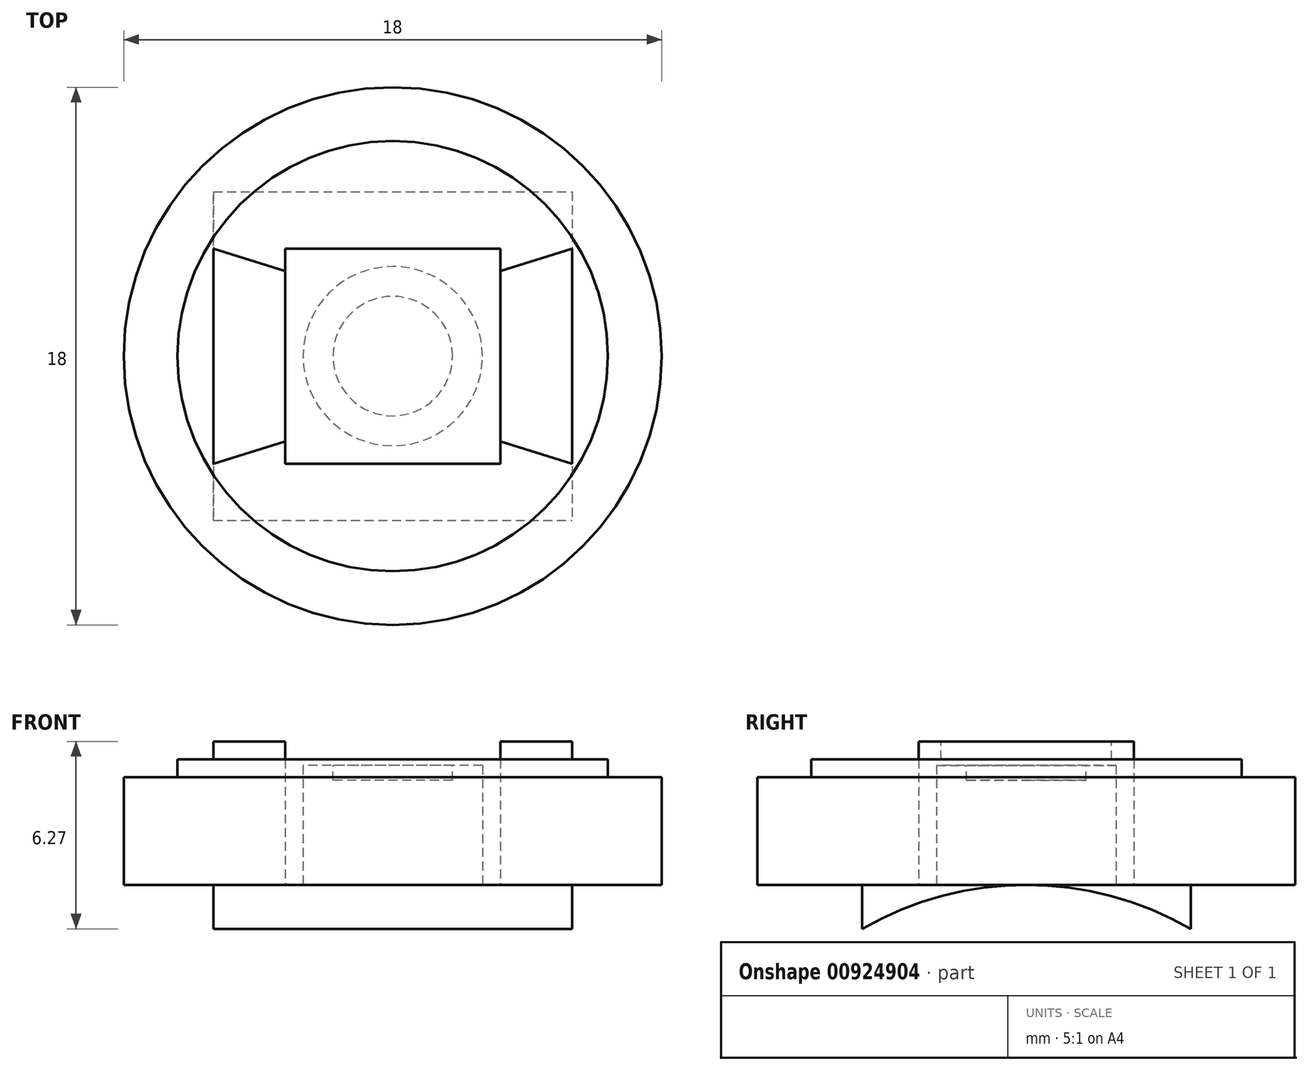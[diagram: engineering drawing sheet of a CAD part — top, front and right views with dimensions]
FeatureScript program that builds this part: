
annotation { "Feature Type Name" : "Feature", "Feature Type Description" : "" }
export const myFeature = defineFeature(function(context is Context, id is Id, definition is map)
    precondition{}
    {
        {
            var Q0;
            Q0=qCreatedBy(makeId("Top.planeOp"),FACE);
            var sketch = newSketch(context, id + "F0", { "sketchPlane" : qUnion([Q0])});
            skCircle(sketch, "E0", {"center": v(0, 0) * mm, "radius": 7.5 * mm});
            skCircle(sketch, "E1", {"center": v(0, 0) * mm, "radius": 6 * mm});
            skCircle(sketch, "E2", {"center": v(0, 0) * mm, "radius": 3 * mm});
            skLineSegment(sketch, "E3", {"start": v(0, 7.5) * mm, "end": v(0, 0) * mm});
            skLineSegment(sketch, "E4", {"start": v(0, 0) * mm, "end": v(0, -7.5) * mm});
            skLineSegment(sketch, "E5", {"start": v(0, 0) * mm, "end": v(7.5, 0) * mm});
            skLineSegment(sketch, "E6", {"start": v(0, 0) * mm, "end": v(-7.5, 0) * mm});
            skLineSegment(sketch, "E7.bottom", {"start": v(3, 3) * mm, "end": v(-3, 3) * mm});
            skLineSegment(sketch, "E7.top", {"start": v(3, -3) * mm, "end": v(-3, -3) * mm});
            skLineSegment(sketch, "E7.left", {"start": v(3, 3) * mm, "end": v(3, -3) * mm});
            skLineSegment(sketch, "E7.right", {"start": v(-3, 3) * mm, "end": v(-3, -3) * mm});
            skLineSegment(sketch, "E8.bottom", {"start": v(-3, 3) * mm, "end": v(3, 3) * mm});
            skLineSegment(sketch, "E8.top", {"start": v(-3, 5) * mm, "end": v(3, 5) * mm});
            skLineSegment(sketch, "E8.left", {"start": v(-3, 3) * mm, "end": v(-3, 5) * mm});
            skLineSegment(sketch, "E8.right", {"start": v(3, 3) * mm, "end": v(3, 5) * mm});
            skLineSegment(sketch, "E9.bottom", {"start": v(-3, -3) * mm, "end": v(3, -3) * mm});
            skLineSegment(sketch, "E9.top", {"start": v(-3, -5) * mm, "end": v(3, -5) * mm});
            skLineSegment(sketch, "E9.left", {"start": v(-3, -3) * mm, "end": v(-3, -5) * mm});
            skLineSegment(sketch, "E9.right", {"start": v(3, -3) * mm, "end": v(3, -5) * mm});
            skSolve(sketch);
        }
        {
            var Q0;
            {var subQ0=sQuery(id+"F0.wireOp",EDGE,"E4");var subQ1=sQuery(id+"F0.wireOp",EDGE,"E0");var subQ2=makeQuery(id+"F0.imprint","INTERSECT",VERTEX,{"derivedFrom":[subQ1,subQ0]});Q0=makeQuery(id+"F0.imprint","IMPRINT",FACE,{"disambiguationData":[TD([[makeQuery(id+"F0.imprint","IMPRINT",EDGE,{"disambiguationData":[TD([[subQ2,-1.0]])],"derivedFrom":subQ1}),1.0]])]});}
            var Q1;
            {var subQ0=sQuery(id+"F0.wireOp",EDGE,"E4");var subQ1=sQuery(id+"F0.wireOp",EDGE,"E0");var subQ2=makeQuery(id+"F0.imprint","INTERSECT",VERTEX,{"derivedFrom":[subQ1,subQ0]});Q1=makeQuery(id+"F0.imprint","IMPRINT",FACE,{"disambiguationData":[TD([[makeQuery(id+"F0.imprint","IMPRINT",EDGE,{"disambiguationData":[TD([[subQ2,1.0]])],"derivedFrom":subQ1}),1.0]])]});}
            var Q2;
            {var subQ0=sQuery(id+"F0.wireOp",EDGE,"E3");var subQ1=sQuery(id+"F0.wireOp",EDGE,"E0");var subQ2=makeQuery(id+"F0.imprint","INTERSECT",VERTEX,{"derivedFrom":[subQ1,subQ0]});Q2=makeQuery(id+"F0.imprint","IMPRINT",FACE,{"disambiguationData":[TD([[makeQuery(id+"F0.imprint","IMPRINT",EDGE,{"disambiguationData":[TD([[subQ2,-1.0]])],"derivedFrom":subQ1}),1.0]])]});}
            var Q3;
            {var subQ0=sQuery(id+"F0.wireOp",EDGE,"E3");var subQ1=sQuery(id+"F0.wireOp",EDGE,"E0");var subQ2=makeQuery(id+"F0.imprint","INTERSECT",VERTEX,{"derivedFrom":[subQ1,subQ0]});Q3=makeQuery(id+"F0.imprint","IMPRINT",FACE,{"disambiguationData":[TD([[makeQuery(id+"F0.imprint","IMPRINT",EDGE,{"disambiguationData":[TD([[subQ2,1.0]])],"derivedFrom":subQ1}),1.0]])]});}
            extrude(context, id + "F1", {"entities" : qUnion([Q0, Q1, Q2, Q3]), "depth" : 3 * mm, "offsetDistance" : 25 * mm});
        }
        {
            var Q0;
            {var subQ9=sQuery(id+"F0.wireOp",EDGE,"E9.right");Q0=makeQuery(id+"F0.imprint","IMPRINT",FACE,{"disambiguationData":[TD([[makeQuery(id+"F0.imprint","IMPRINT",EDGE,{"derivedFrom":subQ9}),1.0]])]});}
            var Q1;
            {var subQ0=sQuery(id+"F0.wireOp",EDGE,"E8.right");Q1=makeQuery(id+"F0.imprint","IMPRINT",FACE,{"disambiguationData":[TD([[makeQuery(id+"F0.imprint","IMPRINT",EDGE,{"derivedFrom":subQ0}),-1.0]])]});}
            var Q2;
            {var subQ9=sQuery(id+"F0.wireOp",EDGE,"E8.left");Q2=makeQuery(id+"F0.imprint","IMPRINT",FACE,{"disambiguationData":[TD([[makeQuery(id+"F0.imprint","IMPRINT",EDGE,{"derivedFrom":subQ9}),1.0]])]});}
            var Q3;
            {var subQ0=sQuery(id+"F0.wireOp",EDGE,"E9.left");Q3=makeQuery(id+"F0.imprint","IMPRINT",FACE,{"disambiguationData":[TD([[makeQuery(id+"F0.imprint","IMPRINT",EDGE,{"derivedFrom":subQ0}),-1.0]])]});}
            extrude(context, id + "F2", {"entities" : qUnion([Q0, Q1, Q2, Q3]), "operationType" : NewBodyOperationType.ADD, "depth" : 3.5 * mm, "offsetDistance" : 25 * mm});
        }
        {
            var Q0;
            {var subQ0=sQuery(id+"F0.wireOp",EDGE,"E5");var subQ1=sQuery(id+"F0.wireOp",EDGE,"E2");var subQ2=makeQuery(id+"F0.imprint","INTERSECT",VERTEX,{"derivedFrom":[subQ1,subQ0,sQuery(id+"F0.wireOp",EDGE,"E7.left")]});Q0=makeQuery(id+"F0.imprint","IMPRINT",FACE,{"disambiguationData":[TD([[makeQuery(id+"F0.imprint","IMPRINT",EDGE,{"disambiguationData":[TD([[subQ2,1.0]])],"derivedFrom":subQ1}),1.0]])]});}
            var Q1;
            {var subQ5=sQuery(id+"F0.wireOp",EDGE,"E9.right");Q1=makeQuery(id+"F0.imprint","IMPRINT",FACE,{"disambiguationData":[TD([[makeQuery(id+"F0.imprint","IMPRINT",EDGE,{"derivedFrom":subQ5}),-1.0]])]});}
            var Q2;
            {var subQ5=sQuery(id+"F0.wireOp",EDGE,"E9.left");Q2=makeQuery(id+"F0.imprint","IMPRINT",FACE,{"disambiguationData":[TD([[makeQuery(id+"F0.imprint","IMPRINT",EDGE,{"derivedFrom":subQ5}),1.0]])]});}
            var Q3;
            {var subQ0=sQuery(id+"F0.wireOp",EDGE,"E6");var subQ1=sQuery(id+"F0.wireOp",EDGE,"E2");var subQ2=makeQuery(id+"F0.imprint","INTERSECT",VERTEX,{"derivedFrom":[subQ1,subQ0,sQuery(id+"F0.wireOp",EDGE,"E7.right")]});Q3=makeQuery(id+"F0.imprint","IMPRINT",FACE,{"disambiguationData":[TD([[makeQuery(id+"F0.imprint","IMPRINT",EDGE,{"disambiguationData":[TD([[subQ2,-1.0]])],"derivedFrom":subQ1}),1.0]])]});}
            var Q4;
            {var subQ0=sQuery(id+"F0.wireOp",EDGE,"E3");var subQ1=sQuery(id+"F0.wireOp",EDGE,"E2");var subQ2=makeQuery(id+"F0.imprint","INTERSECT",VERTEX,{"derivedFrom":[subQ1,subQ0,sQuery(id+"F0.wireOp",EDGE,"E8.bottom")]});Q4=makeQuery(id+"F0.imprint","IMPRINT",FACE,{"disambiguationData":[TD([[makeQuery(id+"F0.imprint","IMPRINT",EDGE,{"disambiguationData":[TD([[subQ2,-1.0]])],"derivedFrom":subQ1}),1.0]])]});}
            var Q5;
            {var subQ5=sQuery(id+"F0.wireOp",EDGE,"E8.right");Q5=makeQuery(id+"F0.imprint","IMPRINT",FACE,{"disambiguationData":[TD([[makeQuery(id+"F0.imprint","IMPRINT",EDGE,{"derivedFrom":subQ5}),1.0]])]});}
            var Q6;
            {var subQ5=sQuery(id+"F0.wireOp",EDGE,"E8.left");Q6=makeQuery(id+"F0.imprint","IMPRINT",FACE,{"disambiguationData":[TD([[makeQuery(id+"F0.imprint","IMPRINT",EDGE,{"derivedFrom":subQ5}),-1.0]])]});}
            var Q7;
            {var subQ0=sQuery(id+"F0.wireOp",EDGE,"E3");var subQ1=sQuery(id+"F0.wireOp",EDGE,"E2");var subQ2=makeQuery(id+"F0.imprint","INTERSECT",VERTEX,{"derivedFrom":[subQ1,subQ0,sQuery(id+"F0.wireOp",EDGE,"E8.bottom")]});Q7=makeQuery(id+"F0.imprint","IMPRINT",FACE,{"disambiguationData":[TD([[makeQuery(id+"F0.imprint","IMPRINT",EDGE,{"disambiguationData":[TD([[subQ2,1.0]])],"derivedFrom":subQ1}),1.0]])]});}
            extrude(context, id + "F3", {"entities" : qUnion([Q0, Q1, Q2, Q3, Q4, Q5, Q6, Q7]), "operationType" : NewBodyOperationType.ADD, "depth" : 4 * mm, "offsetDistance" : 25 * mm});
        }
        {
            var Q0;
            Q0=makeQuery(id+"F2.opExtrude","CAP_FACE",FACE,{"disambiguationData":[OSD([sQuery(id+"F0.wireOp",EDGE,"E1"),sQuery(id+"F0.wireOp",EDGE,"E7.left"),sQuery(id+"F0.wireOp",EDGE,"E7.right"),sQuery(id+"F0.wireOp",EDGE,"E8.top"),sQuery(id+"F0.wireOp",EDGE,"E8.left"),sQuery(id+"F0.wireOp",EDGE,"E8.right"),sQuery(id+"F0.wireOp",EDGE,"E9.top"),sQuery(id+"F0.wireOp",EDGE,"E9.left"),sQuery(id+"F0.wireOp",EDGE,"E9.right")])],"isStart":false});
            var sketch = newSketch(context, id + "F4", { "sketchPlane" : qUnion([Q0])});
            skLineSegment(sketch, "E10.bottom", {"start": v(3, -3) * mm, "end": v(-3, -3) * mm});
            skLineSegment(sketch, "E10.top", {"start": v(3, 3) * mm, "end": v(-3, 3) * mm});
            skLineSegment(sketch, "E10.left", {"start": v(3, -3) * mm, "end": v(3, 3) * mm});
            skLineSegment(sketch, "E10.right", {"start": v(-3, -3) * mm, "end": v(-3, 3) * mm});
            skPoint(sketch, "E10.middle", {"position": v(0, 0) * mm});
            skSolve(sketch);
        }
        {
            var Q0;
            Q0=makeQuery(id+"F4.imprint","IMPRINT",FACE,{"disambiguationData":[TD([[makeQuery(id+"F4.imprint","IMPRINT",EDGE,{"derivedFrom":sQuery(id+"F4.wireOp",EDGE,"E10.bottom")}),-1.0]])]});
            extrude(context, id + "F5", {"entities" : qUnion([Q0]), "oppositeDirection" : true, "depth" : 3.5 * mm, "offsetDistance" : 25 * mm});
        }
        {
            var Q0;
            Q0=makeQuery(id+"F5.opExtrude","SWEPT_BODY",BODY,{"disambiguationData":[OSD([sQuery(id+"F4.wireOp",EDGE,"E10.bottom"),sQuery(id+"F4.wireOp",EDGE,"E10.top"),sQuery(id+"F4.wireOp",EDGE,"E10.left"),sQuery(id+"F4.wireOp",EDGE,"E10.right")])]});
            deleteBodies(context, id + "F6", {"entities" : qUnion([Q0])});
        }
        {
            var Q0;
            Q0=makeQuery(id+"F2.opExtrude","SWEPT_FACE",FACE,{"disambiguationData":[OSD([sQuery(id+"F0.wireOp",EDGE,"E7.right"),sQuery(id+"F0.wireOp",EDGE,"E8.left"),sQuery(id+"F0.wireOp",EDGE,"E9.left")])]});
            extrude(context, id + "F7", {"entities" : qUnion([Q0]), "depth" : 6 * mm, "offsetDistance" : 25 * mm});
        }
        {
            var Q0;
            Q0=makeQuery(id+"F3.opExtrude","CAP_FACE",FACE,{"disambiguationData":[OSD([sQuery(id+"F0.wireOp",EDGE,"E2")])],"isStart":false});
            var Q1;
            Q1=makeQuery(id+"F3.opExtrude","CAP_FACE",FACE,{"disambiguationData":[OSD([sQuery(id+"F0.wireOp",EDGE,"E2")])],"isStart":false});
            var sketch = newSketch(context, id + "F8", { "sketchPlane" : qUnion([Q0, Q1])});
            skCircle(sketch, "E11", {"center": v(0, 0) * mm, "radius": 2 * mm});
            skSolve(sketch);
        }
        {
            var Q0;
            Q0=makeQuery(id+"F8.imprint","IMPRINT",FACE,{"disambiguationData":[TD([[makeQuery(id+"F8.imprint","IMPRINT",EDGE,{"derivedFrom":sQuery(id+"F8.wireOp",EDGE,"E11")}),1.0]])]});
            extrude(context, id + "F9", {"entities" : qUnion([Q0]), "operationType" : NewBodyOperationType.REMOVE, "oppositeDirection" : true, "depth" : .5 * mm, "offsetDistance" : 25 * mm});
        }
        {
            var Q0;
            Q0=qCreatedBy(makeId("Top.planeOp"),FACE);
            var sketch = newSketch(context, id + "F10", { "sketchPlane" : qUnion([Q0])});
            skLineSegment(sketch, "E12.bottom", {"start": v(-27.27, 18.9) * mm, "end": v(-21.27, 18.9) * mm});
            skLineSegment(sketch, "E12.top", {"start": v(-27.27, 12.9) * mm, "end": v(-21.27, 12.9) * mm});
            skLineSegment(sketch, "E12.left", {"start": v(-27.27, 18.9) * mm, "end": v(-27.27, 12.9) * mm});
            skLineSegment(sketch, "E12.right", {"start": v(-21.27, 18.9) * mm, "end": v(-21.27, 12.9) * mm});
            skCircle(sketch, "E13", {"center": v(-24.27, 15.9) * mm, "radius": 3 * mm});
            skSolve(sketch);
        }
        {
            var Q0;
            {var subQ0=sQuery(id+"F10.wireOp",EDGE,"E12.left");var subQ1=sQuery(id+"F10.wireOp",EDGE,"E12.top");var subQ2=makeQuery(id+"F10.imprint","INTERSECT",VERTEX,{"derivedFrom":[subQ1,subQ0]});Q0=makeQuery(id+"F10.imprint","IMPRINT",FACE,{"disambiguationData":[TD([[makeQuery(id+"F10.imprint","IMPRINT",EDGE,{"disambiguationData":[TD([[subQ2,-1.0]])],"derivedFrom":subQ1}),1.0]])]});}
            var Q1;
            {var subQ0=sQuery(id+"F10.wireOp",EDGE,"E12.right");var subQ1=sQuery(id+"F10.wireOp",EDGE,"E12.top");var subQ2=makeQuery(id+"F10.imprint","INTERSECT",VERTEX,{"derivedFrom":[subQ1,subQ0]});Q1=makeQuery(id+"F10.imprint","IMPRINT",FACE,{"disambiguationData":[TD([[makeQuery(id+"F10.imprint","IMPRINT",EDGE,{"disambiguationData":[TD([[subQ2,1.0]])],"derivedFrom":subQ1}),1.0]])]});}
            var Q2;
            {var subQ0=sQuery(id+"F10.wireOp",EDGE,"E12.right");var subQ1=sQuery(id+"F10.wireOp",EDGE,"E12.bottom");var subQ2=makeQuery(id+"F10.imprint","INTERSECT",VERTEX,{"derivedFrom":[subQ1,subQ0]});Q2=makeQuery(id+"F10.imprint","IMPRINT",FACE,{"disambiguationData":[TD([[makeQuery(id+"F10.imprint","IMPRINT",EDGE,{"disambiguationData":[TD([[subQ2,1.0]])],"derivedFrom":subQ1}),-1.0]])]});}
            var Q3;
            {var subQ0=sQuery(id+"F10.wireOp",EDGE,"E12.left");var subQ1=sQuery(id+"F10.wireOp",EDGE,"E12.bottom");var subQ2=makeQuery(id+"F10.imprint","INTERSECT",VERTEX,{"derivedFrom":[subQ1,subQ0]});Q3=makeQuery(id+"F10.imprint","IMPRINT",FACE,{"disambiguationData":[TD([[makeQuery(id+"F10.imprint","IMPRINT",EDGE,{"disambiguationData":[TD([[subQ2,-1.0]])],"derivedFrom":subQ1}),-1.0]])]});}
            extrude(context, id + "F11", {"entities" : qUnion([Q0, Q1, Q2, Q3]), "oppositeDirection" : true, "depth" : 3.5 * mm, "offsetDistance" : 25 * mm});
        }
        {
            var Q0;
            Q0=makeQuery(id+"F11.opExtrude","SWEPT_BODY",BODY,{"disambiguationData":[OSD([sQuery(id+"F10.wireOp",EDGE,"E12.bottom"),sQuery(id+"F10.wireOp",EDGE,"E12.left"),sQuery(id+"F10.wireOp",EDGE,"E13")])]});
            var Q1;
            Q1=makeQuery(id+"F11.opExtrude","SWEPT_BODY",BODY,{"disambiguationData":[OSD([sQuery(id+"F10.wireOp",EDGE,"E12.bottom"),sQuery(id+"F10.wireOp",EDGE,"E12.right"),sQuery(id+"F10.wireOp",EDGE,"E13")])]});
            var Q2;
            Q2=makeQuery(id+"F11.opExtrude","SWEPT_BODY",BODY,{"disambiguationData":[OSD([sQuery(id+"F10.wireOp",EDGE,"E12.top"),sQuery(id+"F10.wireOp",EDGE,"E12.left"),sQuery(id+"F10.wireOp",EDGE,"E13")])]});
            var Q3;
            Q3=makeQuery(id+"F11.opExtrude","SWEPT_BODY",BODY,{"disambiguationData":[OSD([sQuery(id+"F10.wireOp",EDGE,"E12.top"),sQuery(id+"F10.wireOp",EDGE,"E12.right"),sQuery(id+"F10.wireOp",EDGE,"E13")])]});
            deleteBodies(context, id + "F12", {"entities" : qUnion([Q0, Q1, Q2, Q3])});
        }
        {
            var Q0;
            Q0=makeQuery(id+"F1.opExtrude","SWEPT_BODY",BODY,{"disambiguationData":[OSD([sQuery(id+"F0.wireOp",EDGE,"E0"),sQuery(id+"F0.wireOp",EDGE,"E1")])]});
            var Q1;
            Q1=makeQuery(id+"F7.opExtrude","SWEPT_BODY",BODY,{"disambiguationData":[OSD([sQuery(id+"F0.wireOp",EDGE,"E7.right"),sQuery(id+"F0.wireOp",EDGE,"E8.left"),sQuery(id+"F0.wireOp",EDGE,"E9.left")])]});
            var Q2;
            Q2=qCreatedBy(makeId("Origin.pointOp"),VERTEX);
            transform(context, id + "F13", {"entities" : qUnion([Q0, Q1]), "transformType" : TransformType.SCALE_UNIFORMLY, "scale" : 1.2, "scalePoint" : qUnion([Q2]), "makeCopy" : false});
        }
        {
            var Q0;
            Q0=makeQuery(id+"F1.opExtrude","SWEPT_BODY",BODY,{"disambiguationData":[OSD([sQuery(id+"F0.wireOp",EDGE,"E0"),sQuery(id+"F0.wireOp",EDGE,"E1")])]});
            var Q1;
            Q1=makeQuery(id+"F1.opExtrude","CAP_EDGE",EDGE,{"disambiguationData":[OSD([sQuery(id+"F0.wireOp",EDGE,"E0")])],"isStart":false});
            transform(context, id + "F14", {"entities" : qUnion([Q0]), "transformType" : TransformType.ROTATION, "transformAxis" : qUnion([Q1]), "angle" : 90 * degree, "makeCopy" : false});
        }
        {
            var Q0;
            {var subQ0=sQuery(id+"F0.wireOp",EDGE,"E9.right");var subQ1=sQuery(id+"F0.wireOp",EDGE,"E9.left");var subQ2=sQuery(id+"F0.wireOp",EDGE,"E9.top");var subQ3=sQuery(id+"F0.wireOp",EDGE,"E8.right");var subQ4=sQuery(id+"F0.wireOp",EDGE,"E8.left");var subQ5=sQuery(id+"F0.wireOp",EDGE,"E8.top");var subQ6=sQuery(id+"F0.wireOp",EDGE,"E1");Q0=makeQuery(id+"F3.boolean.opBoolean","MERGE",FACE,{"derivedFrom":[makeQuery(id+"F2.boolean.opBoolean","MERGE",FACE,{"derivedFrom":[makeQuery(id+"F1.opExtrude","CAP_FACE",FACE,{"disambiguationData":[OSD([sQuery(id+"F0.wireOp",EDGE,"E0"),subQ6])],"isStart":true}),makeQuery(id+"F2.opExtrude","CAP_FACE",FACE,{"disambiguationData":[OSD([subQ6,sQuery(id+"F0.wireOp",EDGE,"E7.left"),sQuery(id+"F0.wireOp",EDGE,"E7.right"),subQ5,subQ4,subQ3,subQ2,subQ1,subQ0])],"isStart":true})]}),makeQuery(id+"F3.opExtrude","CAP_FACE",FACE,{"disambiguationData":[OSD([sQuery(id+"F0.wireOp",EDGE,"E8.bottom"),subQ5,subQ4,subQ3])],"isStart":true}),makeQuery(id+"F3.opExtrude","CAP_FACE",FACE,{"disambiguationData":[OSD([sQuery(id+"F0.wireOp",EDGE,"E9.bottom"),subQ2,subQ1,subQ0])],"isStart":true})]});}
            var sketch = newSketch(context, id + "F15", { "sketchPlane" : qUnion([Q0])});
            skPoint(sketch, "E14.middle", {"position": v(0, 0) * mm});
            skLineSegment(sketch, "E15.bottom", {"start": v(6, -5.5) * mm, "end": v(-6, -5.5) * mm});
            skLineSegment(sketch, "E15.top", {"start": v(6, 5.5) * mm, "end": v(-6, 5.5) * mm});
            skLineSegment(sketch, "E15.left", {"start": v(6, -5.5) * mm, "end": v(6, 5.5) * mm});
            skLineSegment(sketch, "E15.right", {"start": v(-6, -5.5) * mm, "end": v(-6, 5.5) * mm});
            skSolve(sketch);
        }
        {
            var Q0;
            Q0 = qSketchRegion(id + "F15", true);
            extrude(context, id + "F16", {"entities" : qUnion([Q0]), "depth" : 11 * mm, "offsetDistance" : 25 * mm});
        }
        {
            var Q0;
            Q0=makeQuery(id+"F16.opExtrude","SWEPT_FACE",FACE,{"disambiguationData":[OSD([sQuery(id+"F15.wireOp",EDGE,"E15.left")])]});
            var sketch = newSketch(context, id + "F17", { "sketchPlane" : qUnion([Q0])});
            skCircle(sketch, "E16", {"center": v(0, -11) * mm, "radius": 11 * mm});
            skSolve(sketch);
        }
        {
            var Q0;
            Q0 = qSketchRegion(id + "F17", true);
            var Q1;
            Q1=makeQuery(id+"F16.opExtrude","SWEPT_FACE",FACE,{"disambiguationData":[OSD([sQuery(id+"F15.wireOp",EDGE,"E15.right")])]});
            extrude(context, id + "F18", {"entities" : qUnion([Q0]), "operationType" : NewBodyOperationType.REMOVE, "endBound" : BoundingType.UP_TO_SURFACE, "oppositeDirection" : true, "depth" : 12 * mm, "endBoundEntityFace" : qUnion([Q1]), "offsetDistance" : 25 * mm});
        }
        {
            var Q0;
            Q0=makeQuery(id+"F3.opExtrude","CAP_FACE",FACE,{"disambiguationData":[OSD([sQuery(id+"F0.wireOp",EDGE,"E9.bottom"),sQuery(id+"F0.wireOp",EDGE,"E9.top"),sQuery(id+"F0.wireOp",EDGE,"E9.left"),sQuery(id+"F0.wireOp",EDGE,"E9.right")])],"isStart":false});
            var sketch = newSketch(context, id + "F19", { "sketchPlane" : qUnion([Q0])});
            skLineSegment(sketch, "E17", {"start": v(6, 3.6) * mm, "end": v(3.6, 2.85) * mm});
            skLineSegment(sketch, "E18", {"start": v(3.6, 2.85) * mm, "end": v(3.6, 3.6) * mm});
            skLineSegment(sketch, "E19", {"start": v(3.6, 3.6) * mm, "end": v(6, 3.6) * mm});
            skLineSegment(sketch, "E20", {"start": v(6, 0) * mm, "end": v(3.6, 0) * mm});
            skLineSegment(sketch, "E21", {"start": v(0, 3.64) * mm, "end": v(0, 0) * mm});
            skLineSegment(sketch, "E22.MirrorCS", {"start": v(6, -3.6) * mm, "end": v(3.6, -2.85) * mm});
            skLineSegment(sketch, "E23.MirrorCS", {"start": v(3.6, -3.6) * mm, "end": v(6, -3.6) * mm});
            skLineSegment(sketch, "E24.MirrorCS", {"start": v(3.6, -2.85) * mm, "end": v(3.6, -3.6) * mm});
            skLineSegment(sketch, "E25.MirrorCS", {"start": v(-6, 3.6) * mm, "end": v(-3.6, 2.85) * mm});
            skLineSegment(sketch, "E26.MirrorCS", {"start": v(-3.6, 3.6) * mm, "end": v(-6, 3.6) * mm});
            skLineSegment(sketch, "E27.MirrorCS", {"start": v(-3.6, 2.85) * mm, "end": v(-3.6, 3.6) * mm});
            skLineSegment(sketch, "E28.MirrorCS", {"start": v(-6, -3.6) * mm, "end": v(-3.6, -2.85) * mm});
            skLineSegment(sketch, "E29.MirrorCS", {"start": v(-3.6, -3.6) * mm, "end": v(-6, -3.6) * mm});
            skLineSegment(sketch, "E30.MirrorCS", {"start": v(-3.6, -2.85) * mm, "end": v(-3.6, -3.6) * mm});
            skSolve(sketch);
        }
        {
            var Q0;
            Q0=makeQuery(id+"F19.imprint","IMPRINT",FACE,{"disambiguationData":[TD([[makeQuery(id+"F19.imprint","IMPRINT",EDGE,{"derivedFrom":sQuery(id+"F19.wireOp",EDGE,"E17")}),-1.0]])]});
            var Q1;
            Q1=makeQuery(id+"F19.imprint","IMPRINT",FACE,{"disambiguationData":[TD([[makeQuery(id+"F19.imprint","IMPRINT",EDGE,{"derivedFrom":sQuery(id+"F19.wireOp",EDGE,"E22.MirrorCS")}),1.0]])]});
            var Q2;
            Q2=makeQuery(id+"F19.imprint","IMPRINT",FACE,{"disambiguationData":[TD([[makeQuery(id+"F19.imprint","IMPRINT",EDGE,{"derivedFrom":sQuery(id+"F19.wireOp",EDGE,"E28.MirrorCS")}),-1.0]])]});
            var Q3;
            Q3=makeQuery(id+"F19.imprint","IMPRINT",FACE,{"disambiguationData":[TD([[makeQuery(id+"F19.imprint","IMPRINT",EDGE,{"derivedFrom":sQuery(id+"F19.wireOp",EDGE,"E25.MirrorCS")}),1.0]])]});
            var Q4;
            Q4=makeQuery(id+"F2.opExtrude","CAP_FACE",FACE,{"disambiguationData":[OSD([sQuery(id+"F0.wireOp",EDGE,"E1"),sQuery(id+"F0.wireOp",EDGE,"E7.left"),sQuery(id+"F0.wireOp",EDGE,"E7.right"),sQuery(id+"F0.wireOp",EDGE,"E8.top"),sQuery(id+"F0.wireOp",EDGE,"E8.left"),sQuery(id+"F0.wireOp",EDGE,"E8.right"),sQuery(id+"F0.wireOp",EDGE,"E9.top"),sQuery(id+"F0.wireOp",EDGE,"E9.left"),sQuery(id+"F0.wireOp",EDGE,"E9.right")])],"isStart":false});
            extrude(context, id + "F20", {"entities" : qUnion([Q0, Q1, Q2, Q3]), "operationType" : NewBodyOperationType.REMOVE, "endBound" : BoundingType.UP_TO_SURFACE, "oppositeDirection" : true, "depth" : 25 * mm, "endBoundEntityFace" : qUnion([Q4]), "offsetDistance" : 25 * mm});
        }
    });
